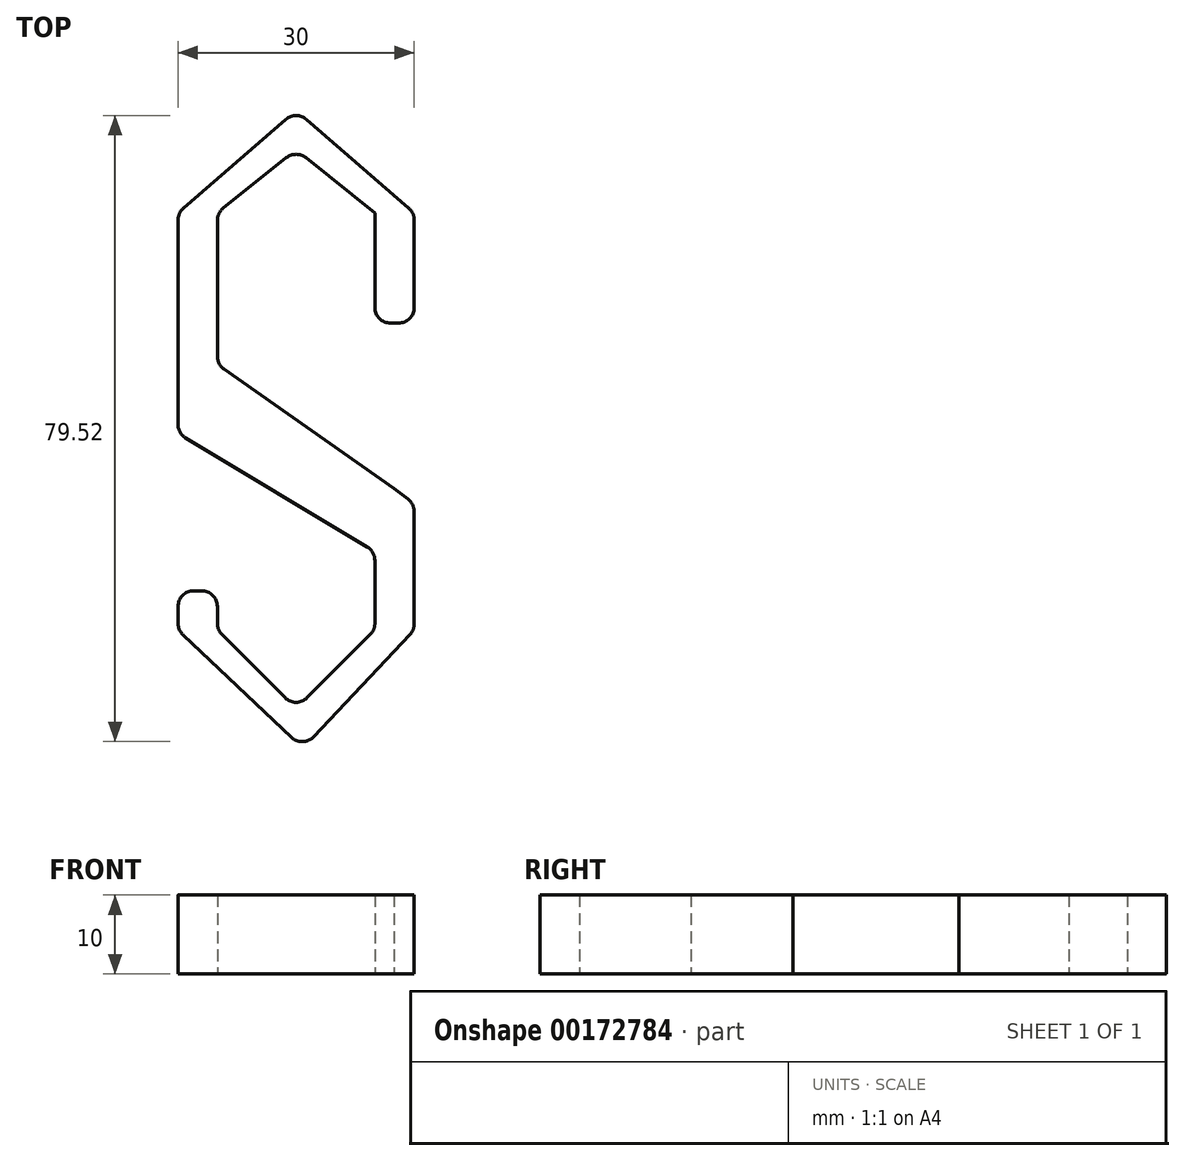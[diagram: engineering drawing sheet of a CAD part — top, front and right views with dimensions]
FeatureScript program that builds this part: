
annotation { "Feature Type Name" : "Feature", "Feature Type Description" : "" }
export const myFeature = defineFeature(function(context is Context, id is Id, definition is map)
    precondition{}
    {
        {
            var Q0;
            Q0=qCreatedBy(makeId("Top.planeOp"),FACE);
            var sketch = newSketch(context, id + "F0", { "sketchPlane" : qUnion([Q0])});
            skLineSegment(sketch, "E0", {"start": v(0, 9.77) * mm, "end": v(0, 27.04) * mm});
            skLineSegment(sketch, "E1", {"start": v(0, 28) * mm, "end": v(20, 28) * mm, "construction": true});
            skLineSegment(sketch, "E2", {"start": v(10, 28) * mm, "end": v(10, 36) * mm, "construction": true});
            skLineSegment(sketch, "E3", {"start": v(0.75, 28.6) * mm, "end": v(8.75, 35) * mm});
            skLineSegment(sketch, "E4", {"start": v(11.25, 35) * mm, "end": v(20, 28) * mm});
            skLineSegment(sketch, "E5", {"start": v(20, 28) * mm, "end": v(20, 16) * mm});
            skLineSegment(sketch, "E6", {"start": v(22, 14) * mm, "end": v(23, 14) * mm});
            skLineSegment(sketch, "E7", {"start": v(25, 16) * mm, "end": v(25, 27.09) * mm});
            skLineSegment(sketch, "E8", {"start": v(10, 36) * mm, "end": v(10, 41) * mm, "construction": true});
            skLineSegment(sketch, "E9", {"start": v(24.3, 28.6) * mm, "end": v(11.3, 39.86) * mm});
            skLineSegment(sketch, "E10", {"start": v(0, 28) * mm, "end": v(-5, 28) * mm, "construction": true});
            skLineSegment(sketch, "E11", {"start": v(8.7, 39.86) * mm, "end": v(-4.3, 28.6) * mm});
            skLineSegment(sketch, "E12", {"start": v(-5, 27.09) * mm, "end": v(-5, 1.13) * mm});
            skPoint(sketch, "E13.visualSharp", {"position": v(20, 14) * mm});
            skArc(sketch, "E13.filletArc", {"start": v(20, 16) * mm, "mid": v(20.59, 14.59) * mm, "end": v(22, 14) * mm});
            skPoint(sketch, "E14.visualSharp", {"position": v(25, 14) * mm});
            skArc(sketch, "E14.filletArc", {"start": v(23, 14) * mm, "mid": v(24.41, 14.59) * mm, "end": v(25, 16) * mm});
            skPoint(sketch, "E15.visualSharp", {"position": v(25, 28) * mm});
            skArc(sketch, "E15.filletArc", {"start": v(25, 27.09) * mm, "mid": v(24.82, 27.92) * mm, "end": v(24.3, 28.6) * mm});
            skPoint(sketch, "E16.visualSharp", {"position": v(10, 41) * mm});
            skArc(sketch, "E16.filletArc", {"start": v(11.3, 39.86) * mm, "mid": v(10, 40.35) * mm, "end": v(8.7, 39.86) * mm});
            skPoint(sketch, "E17.visualSharp", {"position": v(10, 36) * mm});
            skArc(sketch, "E17.filletArc", {"start": v(11.25, 35) * mm, "mid": v(10, 35.44) * mm, "end": v(8.75, 35) * mm});
            skPoint(sketch, "E18.visualSharp", {"position": v(0, 28) * mm});
            skArc(sketch, "E18.filletArc", {"start": v(0.75, 28.6) * mm, "mid": v(0.2, 27.9) * mm, "end": v(0, 27.04) * mm});
            skPoint(sketch, "E19.visualSharp", {"position": v(-5, 28) * mm});
            skArc(sketch, "E19.filletArc", {"start": v(-4.3, 28.6) * mm, "mid": v(-4.82, 27.92) * mm, "end": v(-5, 27.09) * mm});
            skLineSegment(sketch, "E20", {"start": v(-5, 0) * mm, "end": v(20, 0) * mm, "construction": true});
            skPoint(sketch, "E21.startSnap0", {"position": v(25, -0.62) * mm});
            skLineSegment(sketch, "E22", {"start": v(20, 0) * mm, "end": v(20, -15) * mm, "construction": true});
            skLineSegment(sketch, "E23", {"start": v(-4.03, -0.58) * mm, "end": v(19.03, -14.42) * mm});
            skLineSegment(sketch, "E24", {"start": v(20, -16.13) * mm, "end": v(20, -24.17) * mm});
            skLineSegment(sketch, "E25", {"start": v(25, -9.96) * mm, "end": v(25, -24.2) * mm});
            skLineSegment(sketch, "E26", {"start": v(20, -25) * mm, "end": v(10, -25) * mm, "construction": true});
            skLineSegment(sketch, "E27", {"start": v(10, -25) * mm, "end": v(10, -35) * mm, "construction": true});
            skLineSegment(sketch, "E28", {"start": v(19.41, -25.59) * mm, "end": v(11.41, -33.59) * mm});
            skLineSegment(sketch, "E29", {"start": v(10, -35) * mm, "end": v(10, -40) * mm, "construction": true});
            skLineSegment(sketch, "E30", {"start": v(12.22, -38.54) * mm, "end": v(24.45, -25.58) * mm});
            skLineSegment(sketch, "E31", {"start": v(20, -25) * mm, "end": v(0, -25) * mm, "construction": true});
            skLineSegment(sketch, "E32", {"start": v(0, -25) * mm, "end": v(-5, -25) * mm, "construction": true});
            skLineSegment(sketch, "E33", {"start": v(-4.37, -25.6) * mm, "end": v(9.4, -38.62) * mm});
            skLineSegment(sketch, "E34", {"start": v(8.59, -33.59) * mm, "end": v(0.59, -25.59) * mm});
            skLineSegment(sketch, "E35", {"start": v(-5, -24.14) * mm, "end": v(-5, -22) * mm});
            skLineSegment(sketch, "E36", {"start": v(-3, -20) * mm, "end": v(-2, -20) * mm});
            skLineSegment(sketch, "E37", {"start": v(0, -22) * mm, "end": v(0, -24.17) * mm});
            skPoint(sketch, "E38.visualSharp", {"position": v(-5, 0) * mm});
            skArc(sketch, "E38.filletArc", {"start": v(-5, 1.13) * mm, "mid": v(-4.74, 0.15) * mm, "end": v(-4.03, -0.58) * mm});
            skPoint(sketch, "E39.visualSharp", {"position": v(0, 0) * mm});
            skPoint(sketch, "E40.visualSharp", {"position": v(25, -10) * mm});
            skPoint(sketch, "E41.visualSharp", {"position": v(20, -15) * mm});
            skArc(sketch, "E41.filletArc", {"start": v(20, -16.13) * mm, "mid": v(19.74, -15.15) * mm, "end": v(19.03, -14.42) * mm});
            skPoint(sketch, "E42.visualSharp", {"position": v(20, -25) * mm});
            skArc(sketch, "E42.filletArc", {"start": v(19.41, -25.59) * mm, "mid": v(19.85, -24.94) * mm, "end": v(20, -24.17) * mm});
            skPoint(sketch, "E43.visualSharp", {"position": v(25, -25) * mm});
            skArc(sketch, "E43.filletArc", {"start": v(24.45, -25.58) * mm, "mid": v(24.86, -24.94) * mm, "end": v(25, -24.2) * mm});
            skPoint(sketch, "E44.visualSharp", {"position": v(10.85, -40) * mm});
            skArc(sketch, "E44.filletArc", {"start": v(9.4, -38.62) * mm, "mid": v(10.82, -39.17) * mm, "end": v(12.22, -38.54) * mm});
            skPoint(sketch, "E45.visualSharp", {"position": v(10, -35) * mm});
            skArc(sketch, "E45.filletArc", {"start": v(8.59, -33.59) * mm, "mid": v(10, -34.17) * mm, "end": v(11.41, -33.59) * mm});
            skPoint(sketch, "E46.visualSharp", {"position": v(0, -25) * mm});
            skArc(sketch, "E46.filletArc", {"start": v(0, -24.17) * mm, "mid": v(0.15, -24.94) * mm, "end": v(0.59, -25.59) * mm});
            skPoint(sketch, "E47.visualSharp", {"position": v(0, -20) * mm});
            skArc(sketch, "E47.filletArc", {"start": v(0, -22) * mm, "mid": v(-0.59, -20.59) * mm, "end": v(-2, -20) * mm});
            skPoint(sketch, "E48.visualSharp", {"position": v(-5, -20) * mm});
            skArc(sketch, "E48.filletArc", {"start": v(-3, -20) * mm, "mid": v(-4.41, -20.59) * mm, "end": v(-5, -22) * mm});
            skPoint(sketch, "E49.visualSharp", {"position": v(-5, -25) * mm});
            skArc(sketch, "E49.filletArc", {"start": v(-5, -24.14) * mm, "mid": v(-4.84, -24.93) * mm, "end": v(-4.37, -25.6) * mm});
            skLineSegment(sketch, "E50", {"start": v(0.85, 8.14) * mm, "end": v(22.47, -7.04) * mm});
            skPoint(sketch, "E51.visualSharp", {"position": v(0, 8.73) * mm});
            skArc(sketch, "E51.filletArc", {"start": v(0, 9.77) * mm, "mid": v(0.23, 8.85) * mm, "end": v(0.85, 8.14) * mm});
            skLineSegment(sketch, "E52", {"start": v(22.47, -7.04) * mm, "end": v(24.21, -8.37) * mm});
            skPoint(sketch, "E53.visualSharp", {"position": v(25, -8.97) * mm});
            skArc(sketch, "E53.filletArc", {"start": v(25, -9.96) * mm, "mid": v(24.8, -9.07) * mm, "end": v(24.21, -8.37) * mm});
            skSolve(sketch);
        }
        {
            var Q0;
            Q0=makeQuery(id+"F0.imprint","IMPRINT",FACE,{"disambiguationData":[TD([[makeQuery(id+"F0.imprint","IMPRINT",EDGE,{"derivedFrom":sQuery(id+"F0.wireOp",EDGE,"E0")}),1.0]])]});
            extrude(context, id + "F1", {"entities" : qUnion([Q0]), "depth" : 10 * mm});
        }
    });
